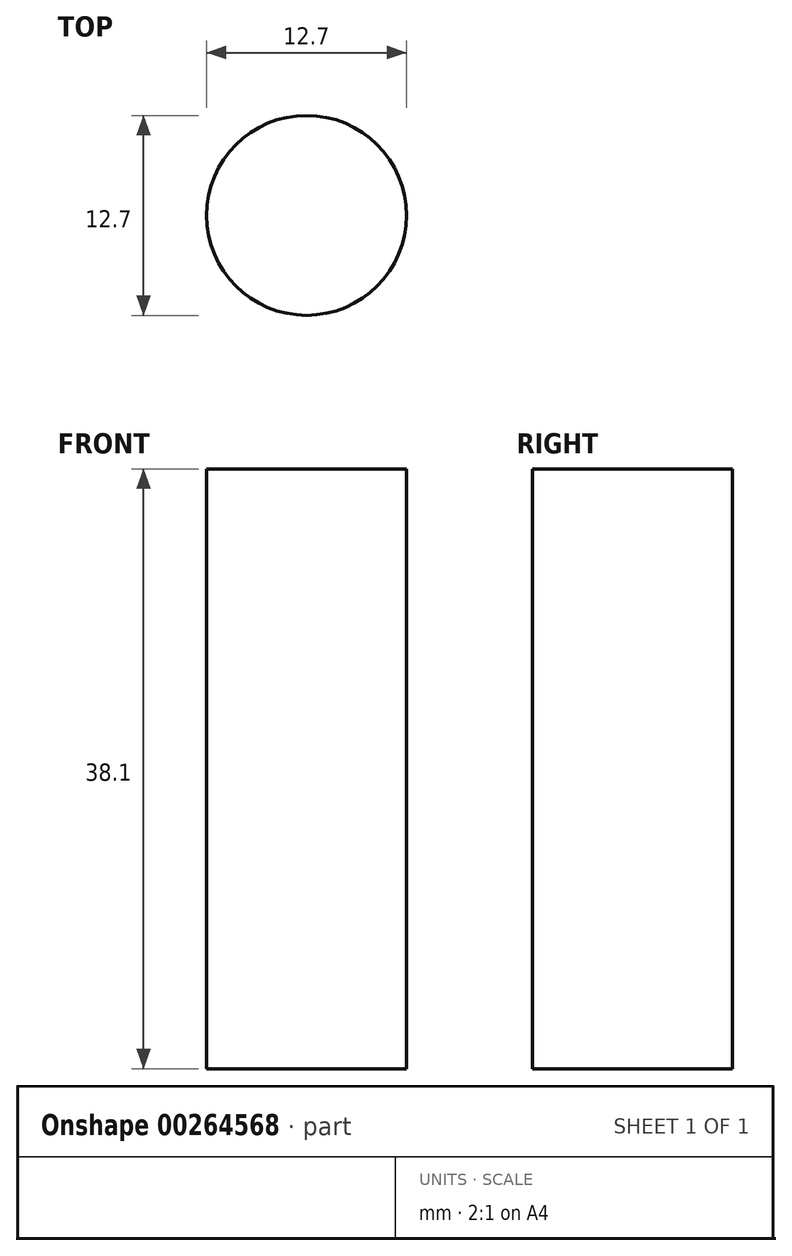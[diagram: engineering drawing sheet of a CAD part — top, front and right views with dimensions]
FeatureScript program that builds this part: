
annotation { "Feature Type Name" : "Feature", "Feature Type Description" : "" }
export const myFeature = defineFeature(function(context is Context, id is Id, definition is map)
    precondition{}
    {
        {
            var Q0;
            Q0=qCreatedBy(makeId("Top.planeOp"),FACE);
            var sketch = newSketch(context, id + "F0", { "sketchPlane" : qUnion([Q0])});
            skCircle(sketch, "E0", {"center": v(0, 0) * mm, "radius": 6.35 * mm});
            skSolve(sketch);
        }
        {
            var Q0;
            Q0=makeQuery(id+"F0.imprint","IMPRINT",FACE,{"disambiguationData":[TD([[makeQuery(id+"F0.imprint","IMPRINT",EDGE,{"derivedFrom":sQuery(id+"F0.wireOp",EDGE,"E0")}),1.0]])]});
            extrude(context, id + "F1", {"entities" : qUnion([Q0]), "depth" : 38.1 * mm});
        }
    });
